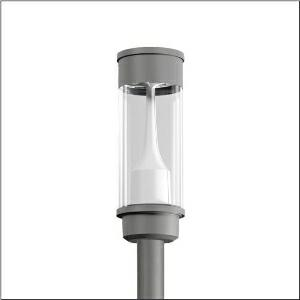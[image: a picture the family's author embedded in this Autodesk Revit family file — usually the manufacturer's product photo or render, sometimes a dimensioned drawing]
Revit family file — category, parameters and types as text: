
# Revit family: litepole_iq___p1_0a_5xa5415ff14h_1a61
name_source: partatom
category: Lighting Fixtures
units: mm (PartAtom-declared; Revit-internal decimal feet)

## family parameters
Cut with Voids When Loaded = No
Host = Face
Light Source = No
Part Type = Normal
Room Calculation Point = No
Round Connector Dimension = Use Diameter
Shared = No

## types (1)
- --- (1 x LED, 1510 lm, 10.5 W, 3000K)
    Apparent Load = 11 VA
    CIE Flux Codes = 32 61 90 93 100
    Color Rendering = 70
    Color Temperature = 3000K
    Default Elevation = 1800 mm
    Description = Litepole, mast luminaire, Module 540 iQ-SR, primary light control with 3 zone facetted reflector, of plastic, silver coated, highly specular, structured, primary optical cover: cover, of PMMA, transparent, light distribution: P1.0a, light emission: direct distribution, primary light characteristic: strongly asymmetric, installation type: post-top, LED, High Power LED, rated luminous flux: 1.510lm, luminous efficacy: 144lm/W, light colour: 730, colour temperature: 3000K, control gear: ECG iQ, control: Auto-Match, Temp-Guard, Lumen-Switch, Night-Set, Smart-Wire, Light-Fading, Desk-Remote (wireless, voltage-free reading and setting of iQ features in the workshop via application-optimized NFC function/RFID function), optimised constant luminous flux control (CLO 2.0), Street-Remote, presetting dimming logarithmic, with terminal, 6-pole, max. 2.5mm², mains connection: 220..240V, AC, 50/60Hz, start of lifetime: 11W, end of lifetime: 11W, reduction: 5W, luminaire housing, upper part, of glass-fibre reinforced polyester, coated, Siteco® metallic grey (DB 702S), diameter: 210mm, height: 590mm, spigot size: d x l = 76 x 70mm (post-top) | with reducer (optional accessory) 60 x 70mm, post-top mast mounting element, of diecast aluminium, coated, Siteco® metallic grey (DB 702S), Module 540 iQ-SR, traffic white (RAL 9016), equipment: standard, protection rating (complete): IP65, insulation class (complete): insulation class II (safety insulation), certification: CE, ENEC, VDE, packaging unit: 1 piece

Light Distribution: P1.0a
    Height = 590 mm
    Lamp = 1 x LED
    Lamp Light Flux = 1510 lm
    Lamp Power = 10.5 W
    Lamp count = 1
    Length = 220 mm
    Luminous efficacy = 144 lm/W
    Manufacturer = Siteco
    ModVariant = No
    Model = 5XA5415FF14H
    Number of Poles = 1
    OnlyDefault = Yes
    Power Factor = 1
    Product Name = Litepole iQ | P1.0a
    Product group = mast luminaire | pylon top
    ProductGroupID = 6100
    Protection Class = Protection class II
    Protection Degree = IP 65
    RLX_Detail_Level = 1
    RlxData = <blob elided: 64093 chars, md5=2a496918>
    Socket = socket
    Standby Power = 0 W
    System Light Flux = 1510 lm
    System Power = 11 W
    Type Comments = factory setting: luminous flux: 100 % | dim-lin: 254 | 419 mA
    Type Image = l_1006025.jpg
    URL = http://relux.com
    VarID = @adj_069975
    Voltage = 0 V
    Weight = 0.00 kg
    Width = 0 mm  [stored 0 ft]

note: [stored X ft] marks values corroborated as IEEE doubles in the binary element streams (Revit-internal decimal feet)

## geometry (parser evidence)
native form markers: Blend x4, Sweep x13
no freeform markers — native parametric forms only
